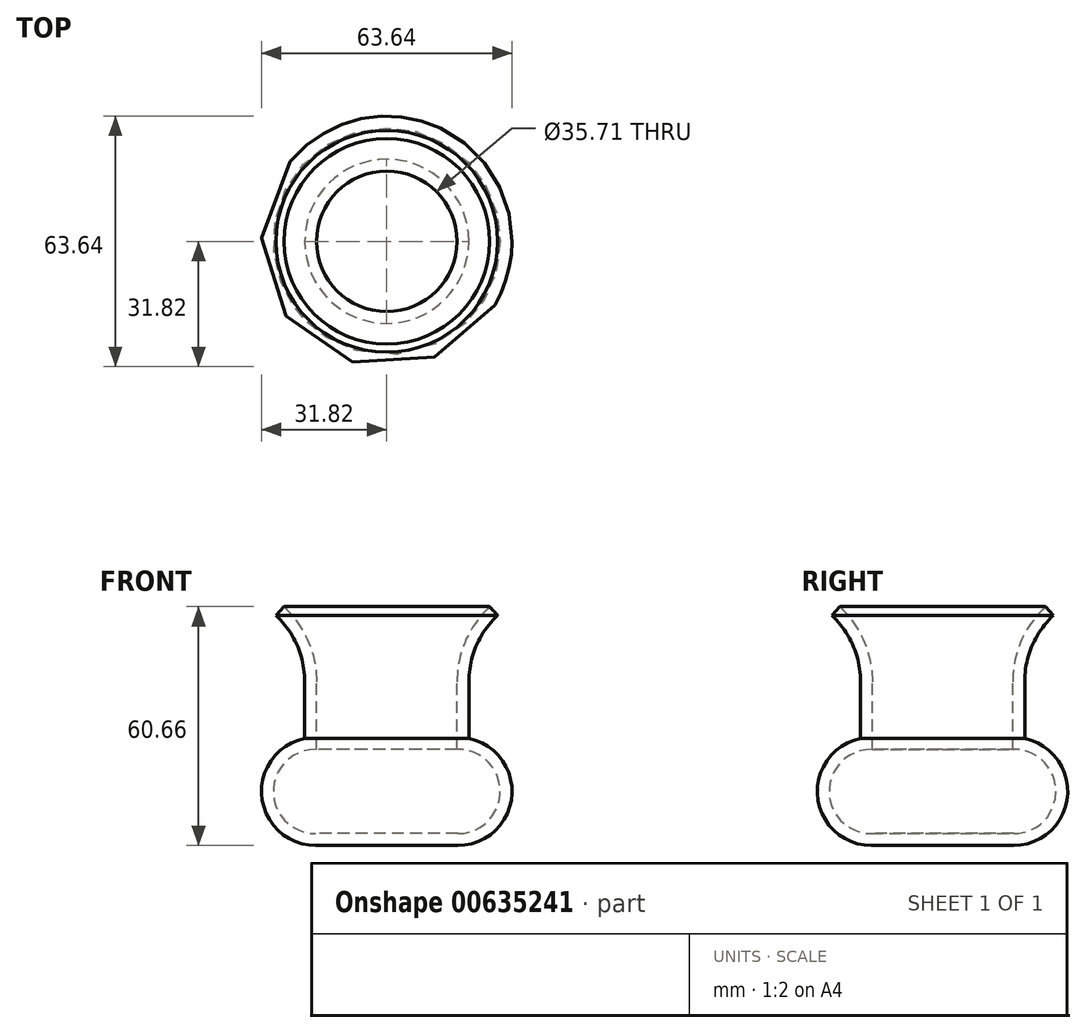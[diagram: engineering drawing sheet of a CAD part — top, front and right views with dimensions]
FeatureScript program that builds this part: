
annotation { "Feature Type Name" : "Feature", "Feature Type Description" : "" }
export const myFeature = defineFeature(function(context is Context, id is Id, definition is map)
    precondition{}
    {
        {
            var Q0;
            Q0=qCreatedBy(makeId("Front.planeOp"),FACE);
            var sketch = newSketch(context, id + "F0", { "sketchPlane" : qUnion([Q0])});
            skLineSegment(sketch, "E0", {"start": v(0, 0) * mm, "end": v(-18.12, 0) * mm});
            skArc(sketch, "E1", {"start": v(-18.12, 0) * mm, "mid": v(-31.75, 12.33) * mm, "end": v(-20.85, 27.13) * mm});
            skLineSegment(sketch, "E2", {"start": v(-20.85, 27.13) * mm, "end": v(-20.85, 41.59) * mm});
            skArc(sketch, "E3", {"start": v(-20.85, 41.59) * mm, "mid": v(-22.76, 50.79) * mm, "end": v(-28.16, 58.47) * mm});
            skArc(sketch, "E4.0", {"start": v(-17.85, 41.59) * mm, "mid": v(-20, 51.98) * mm, "end": v(-26.1, 60.66) * mm});
            skLineSegment(sketch, "E4.1", {"start": v(-17.85, 24.4) * mm, "end": v(-17.85, 41.59) * mm});
            skArc(sketch, "E4.2", {"start": v(-18.12, 3) * mm, "mid": v(-28.82, 13.84) * mm, "end": v(-17.85, 24.4) * mm});
            skLineSegment(sketch, "E4.3", {"start": v(0, 3) * mm, "end": v(-18.12, 3) * mm});
            skLineSegment(sketch, "E5", {"start": v(-28.16, 58.47) * mm, "end": v(-26.1, 60.66) * mm});
            skLineSegment(sketch, "E6", {"start": v(0, 3) * mm, "end": v(0, 0) * mm});
            skSolve(sketch);
        }
        {
            var Q0;
            Q0=makeQuery(id+"F0.imprint","IMPRINT",FACE,{"disambiguationData":[TD([[makeQuery(id+"F0.imprint","IMPRINT",EDGE,{"derivedFrom":sQuery(id+"F0.wireOp",EDGE,"E0")}),-1.0]])]});
            var Q1;
            Q1=sQuery(id+"F0.wireOp",EDGE,"E6");
            revolve(context, id + "F1", {"entities" : qUnion([Q0]), "axis" : qUnion([Q1]), "revolveType" : RevolveType.FULL});
        }
    });
